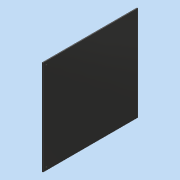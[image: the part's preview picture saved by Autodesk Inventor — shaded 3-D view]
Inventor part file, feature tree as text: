
AUTODESK INVENTOR PART (.ipt)
format: ipt  version: 2016 (Build 200138000, 138)  size: 89,088 bytes
history: native  units: mm
features: hole x2, extrude x1, sketch x1
ambient origin geometry x8: Origin, YZ Plane, XZ Plane, XY Plane, X Axis, Y Axis, Z Axis, Center Point
bodies: Solid1 (feature_tree)
feature tree (4):
  extrude  "Extrusion1"  Depth=360.0mm
  hole  "Hole1"  [1 undecoded]
  hole  "Hole2"  [1 undecoded]
  sketch  "Sketch1"  dims[d0=360.0mm d1=360.0mm d2=3.0mm d3=0.0mm d4=12.0mm d5=12.0mm d6=4.0mm d7=6.0mm d8=4.0mm d9=2.0mm d10=90.0deg d11=8.0mm d12=20.594885mm d13=12.0mm d14=12.0mm d15=4.0mm d16=6.0mm d17=4.0mm d18=2.0mm d19=90.0deg d20=8.0mm d21=20.594885mm]
note: 2 required parameter values undecoded (feature->parameter linkage not recoverable at this tier; creation-order binding heuristic only, values carry confidence <= 0.55)
